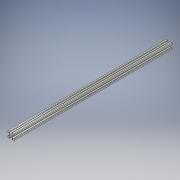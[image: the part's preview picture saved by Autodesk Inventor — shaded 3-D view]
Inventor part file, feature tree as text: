
AUTODESK INVENTOR PART (.ipt)
format: ipt  version: 2019 (Build 230136000, 136)  size: 174,592 bytes
history: native  units: mm
features: extrude x1, sketch x1
ambient origin geometry x8: Origin, YZ Plane, XZ Plane, XY Plane, X Axis, Y Axis, Z Axis, Center Point
bodies: Body1 (feature_tree)
feature tree (2):
  extrude  "Extrusion6"  [1 undecoded]
  sketch  "Sketch1"  dims[d10=500.0mm d11=0.0mm]
note: 1 required parameter value undecoded (feature->parameter linkage not recoverable at this tier; creation-order binding heuristic only, values carry confidence <= 0.55)
